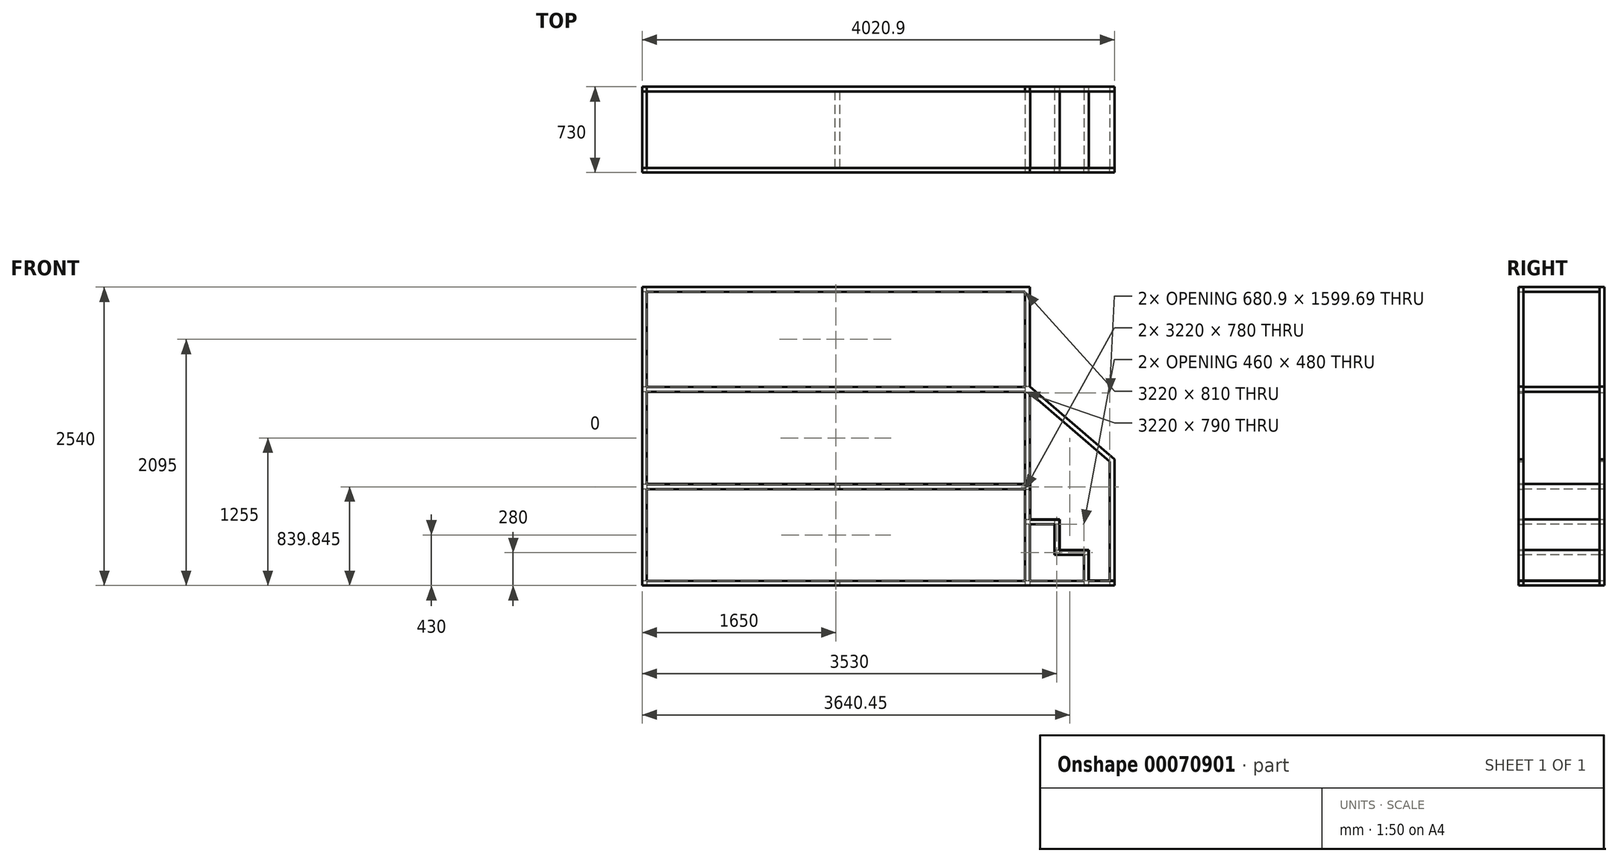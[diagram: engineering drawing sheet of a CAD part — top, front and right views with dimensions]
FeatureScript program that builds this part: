
annotation { "Feature Type Name" : "Feature", "Feature Type Description" : "" }
export const myFeature = defineFeature(function(context is Context, id is Id, definition is map)
    precondition{}
    {
        {
            var Q0;
            Q0=qCreatedBy(makeId("Front.planeOp"),FACE);
            var sketch = newSketch(context, id + "F0", { "sketchPlane" : qUnion([Q0])});
            skLineSegment(sketch, "E0", {"start": v(40, 0) * mm, "end": v(3260, 0) * mm});
            skLineSegment(sketch, "E1.0", {"start": v(40, 40) * mm, "end": v(3260, 40) * mm});
            skLineSegment(sketch, "E2", {"start": v(0, 40) * mm, "end": v(0, 0) * mm});
            skLineSegment(sketch, "E3.0", {"start": v(3300, 40) * mm, "end": v(3300, 0) * mm});
            skLineSegment(sketch, "E4", {"start": v(0, 0) * mm, "end": v(0, -820) * mm});
            skLineSegment(sketch, "E5", {"start": v(3300, 0) * mm, "end": v(3300, -260) * mm});
            skLineSegment(sketch, "E6", {"start": v(0, -820) * mm, "end": v(3300, -820) * mm});
            skLineSegment(sketch, "E7.0", {"start": v(40, -780) * mm, "end": v(3260, -780) * mm});
            skLineSegment(sketch, "E8.0", {"start": v(40, 0) * mm, "end": v(40, -780) * mm});
            skLineSegment(sketch, "E9.0", {"start": v(3260, 0) * mm, "end": v(3260, -780) * mm});
            skLineSegment(sketch, "E10", {"start": v(0, 40) * mm, "end": v(0, 1720) * mm});
            skLineSegment(sketch, "E11", {"start": v(0, 1720) * mm, "end": v(3300, 1720) * mm});
            skLineSegment(sketch, "E12", {"start": v(3300, 1720) * mm, "end": v(3300, 872.37) * mm});
            skLineSegment(sketch, "E13", {"start": v(40, 40) * mm, "end": v(40, 1680) * mm});
            skLineSegment(sketch, "E14", {"start": v(40, 1680) * mm, "end": v(3260, 1680) * mm});
            skLineSegment(sketch, "E15", {"start": v(3260, 1680) * mm, "end": v(3260, 40) * mm});
            skLineSegment(sketch, "E16", {"start": v(3300, 872.37) * mm, "end": v(4020.9, 254.57) * mm});
            skLineSegment(sketch, "E17", {"start": v(4020.9, 254.57) * mm, "end": v(4020.9, -820) * mm});
            skLineSegment(sketch, "E18", {"start": v(4020.9, -820) * mm, "end": v(3300, -820) * mm});
            skLineSegment(sketch, "E19", {"start": v(3260, -780) * mm, "end": v(3760, -780) * mm});
            skLineSegment(sketch, "E20", {"start": v(3980.9, -780) * mm, "end": v(3980.9, 236.17) * mm});
            skLineSegment(sketch, "E21", {"start": v(3980.9, 236.17) * mm, "end": v(3300, 819.7) * mm});
            skLineSegment(sketch, "E22", {"start": v(3300, -300) * mm, "end": v(3510, -300) * mm});
            skLineSegment(sketch, "E23", {"start": v(3510, -300) * mm, "end": v(3510, -560) * mm});
            skLineSegment(sketch, "E24", {"start": v(3510, -560) * mm, "end": v(3760, -560) * mm});
            skLineSegment(sketch, "E25", {"start": v(3760, -560) * mm, "end": v(3760, -780) * mm});
            skLineSegment(sketch, "E26", {"start": v(3300, -260) * mm, "end": v(3550, -260) * mm});
            skLineSegment(sketch, "E27", {"start": v(3550, -260) * mm, "end": v(3550, -520) * mm});
            skLineSegment(sketch, "E28", {"start": v(3550, -520) * mm, "end": v(3800, -520) * mm});
            skLineSegment(sketch, "E29", {"start": v(3800, -520) * mm, "end": v(3800, -780) * mm});
            skLineSegment(sketch, "E30.trimOffspring", {"start": v(3300, -300) * mm, "end": v(3300, -820) * mm});
            skLineSegment(sketch, "E31.trimOffspring", {"start": v(3800, -780) * mm, "end": v(3980.9, -780) * mm});
            skLineSegment(sketch, "E32.trimOffspring", {"start": v(3300, 819.7) * mm, "end": v(3300, 40) * mm});
            skSolve(sketch);
        }
        {
            var Q0;
            Q0=makeQuery(id+"F0.imprint","IMPRINT",FACE,{"disambiguationData":[TD([[makeQuery(id+"F0.imprint","IMPRINT",EDGE,{"derivedFrom":sQuery(id+"F0.wireOp",EDGE,"E0")}),1.0]])]});
            extrude(context, id + "F1", {"entities" : qUnion([Q0]), "depth" : 40 * mm});
        }
        {
            var Q0;
            Q0=makeQuery(id+"F1.opExtrude","CAP_FACE",FACE,{"disambiguationData":[OSD([sQuery(id+"F0.wireOp",EDGE,"E0"),sQuery(id+"F0.wireOp",EDGE,"E1.0"),sQuery(id+"F0.wireOp",EDGE,"E2"),sQuery(id+"F0.wireOp",EDGE,"E3.0"),sQuery(id+"F0.wireOp",EDGE,"E4"),sQuery(id+"F0.wireOp",EDGE,"E5"),sQuery(id+"F0.wireOp",EDGE,"E6"),sQuery(id+"F0.wireOp",EDGE,"E7.0"),sQuery(id+"F0.wireOp",EDGE,"E8.0"),sQuery(id+"F0.wireOp",EDGE,"E9.0"),sQuery(id+"F0.wireOp",EDGE,"E10"),sQuery(id+"F0.wireOp",EDGE,"E11"),sQuery(id+"F0.wireOp",EDGE,"E12"),sQuery(id+"F0.wireOp",EDGE,"E13"),sQuery(id+"F0.wireOp",EDGE,"E14"),sQuery(id+"F0.wireOp",EDGE,"E15"),sQuery(id+"F0.wireOp",EDGE,"E16"),sQuery(id+"F0.wireOp",EDGE,"E17"),sQuery(id+"F0.wireOp",EDGE,"E18"),sQuery(id+"F0.wireOp",EDGE,"E19"),sQuery(id+"F0.wireOp",EDGE,"E20"),sQuery(id+"F0.wireOp",EDGE,"E21"),sQuery(id+"F0.wireOp",EDGE,"E22"),sQuery(id+"F0.wireOp",EDGE,"E23"),sQuery(id+"F0.wireOp",EDGE,"E24"),sQuery(id+"F0.wireOp",EDGE,"E25"),sQuery(id+"F0.wireOp",EDGE,"E26"),sQuery(id+"F0.wireOp",EDGE,"E27"),sQuery(id+"F0.wireOp",EDGE,"E28"),sQuery(id+"F0.wireOp",EDGE,"E29"),sQuery(id+"F0.wireOp",EDGE,"E30.trimOffspring"),sQuery(id+"F0.wireOp",EDGE,"E31.trimOffspring"),sQuery(id+"F0.wireOp",EDGE,"E32.trimOffspring")])],"isStart":true});
            var sketch = newSketch(context, id + "F2", { "sketchPlane" : qUnion([Q0])});
            skLineSegment(sketch, "E33.bottom", {"start": v(-3260, 0) * mm, "end": v(-3300, 0) * mm});
            skLineSegment(sketch, "E33.top", {"start": v(-3260, 40) * mm, "end": v(-3300, 40) * mm});
            skLineSegment(sketch, "E33.left", {"start": v(-3260, 0) * mm, "end": v(-3260, 40) * mm});
            skLineSegment(sketch, "E33.right", {"start": v(-3300, 0) * mm, "end": v(-3300, 40) * mm});
            skLineSegment(sketch, "E34.bottom", {"start": v(-3300, -260) * mm, "end": v(-3260, -260) * mm});
            skLineSegment(sketch, "E34.top", {"start": v(-3300, -300) * mm, "end": v(-3260, -300) * mm});
            skLineSegment(sketch, "E34.left", {"start": v(-3300, -260) * mm, "end": v(-3300, -300) * mm});
            skLineSegment(sketch, "E34.right", {"start": v(-3260, -260) * mm, "end": v(-3260, -300) * mm});
            skLineSegment(sketch, "E35.bottom", {"start": v(-3550, -260) * mm, "end": v(-3510, -260) * mm});
            skLineSegment(sketch, "E35.top", {"start": v(-3550, -300) * mm, "end": v(-3510, -300) * mm});
            skLineSegment(sketch, "E35.left", {"start": v(-3550, -260) * mm, "end": v(-3550, -300) * mm});
            skLineSegment(sketch, "E35.right", {"start": v(-3510, -260) * mm, "end": v(-3510, -300) * mm});
            skLineSegment(sketch, "E36.bottom", {"start": v(-3550, -520) * mm, "end": v(-3510, -520) * mm});
            skLineSegment(sketch, "E36.top", {"start": v(-3550, -560) * mm, "end": v(-3510, -560) * mm});
            skLineSegment(sketch, "E36.left", {"start": v(-3550, -520) * mm, "end": v(-3550, -560) * mm});
            skLineSegment(sketch, "E36.right", {"start": v(-3510, -520) * mm, "end": v(-3510, -560) * mm});
            skLineSegment(sketch, "E37.bottom", {"start": v(-3800, -520) * mm, "end": v(-3760, -520) * mm});
            skLineSegment(sketch, "E37.top", {"start": v(-3800, -560) * mm, "end": v(-3760, -560) * mm});
            skLineSegment(sketch, "E37.left", {"start": v(-3800, -520) * mm, "end": v(-3800, -560) * mm});
            skLineSegment(sketch, "E37.right", {"start": v(-3760, -520) * mm, "end": v(-3760, -560) * mm});
            skLineSegment(sketch, "E38.bottom", {"start": v(-3980.9, -780) * mm, "end": v(-4020.9, -780) * mm});
            skLineSegment(sketch, "E38.top", {"start": v(-3980.9, -820) * mm, "end": v(-4020.9, -820) * mm});
            skLineSegment(sketch, "E38.left", {"start": v(-3980.9, -780) * mm, "end": v(-3980.9, -820) * mm});
            skLineSegment(sketch, "E38.right", {"start": v(-4020.9, -780) * mm, "end": v(-4020.9, -820) * mm});
            skLineSegment(sketch, "E39.bottom", {"start": v(-40, 40) * mm, "end": v(0, 40) * mm});
            skLineSegment(sketch, "E39.top", {"start": v(-40, 0) * mm, "end": v(0, 0) * mm});
            skLineSegment(sketch, "E39.left", {"start": v(-40, 40) * mm, "end": v(-40, 0) * mm});
            skLineSegment(sketch, "E39.right", {"start": v(0, 40) * mm, "end": v(0, 0) * mm});
            skLineSegment(sketch, "E40.bottom", {"start": v(-40, -780) * mm, "end": v(0, -780) * mm});
            skLineSegment(sketch, "E40.top", {"start": v(-40, -820) * mm, "end": v(0, -820) * mm});
            skLineSegment(sketch, "E40.left", {"start": v(-40, -780) * mm, "end": v(-40, -820) * mm});
            skLineSegment(sketch, "E40.right", {"start": v(0, -780) * mm, "end": v(0, -820) * mm});
            skLineSegment(sketch, "E41.bottom", {"start": v(-3800, -780) * mm, "end": v(-3760, -780) * mm});
            skLineSegment(sketch, "E41.top", {"start": v(-3800, -820) * mm, "end": v(-3760, -820) * mm});
            skLineSegment(sketch, "E41.left", {"start": v(-3800, -780) * mm, "end": v(-3800, -820) * mm});
            skLineSegment(sketch, "E41.right", {"start": v(-3760, -780) * mm, "end": v(-3760, -820) * mm});
            skLineSegment(sketch, "E42.bottom", {"start": v(-3300, -780) * mm, "end": v(-3260, -780) * mm});
            skLineSegment(sketch, "E42.top", {"start": v(-3300, -820) * mm, "end": v(-3260, -820) * mm});
            skLineSegment(sketch, "E42.left", {"start": v(-3300, -780) * mm, "end": v(-3300, -820) * mm});
            skLineSegment(sketch, "E42.right", {"start": v(-3260, -780) * mm, "end": v(-3260, -820) * mm});
            skLineSegment(sketch, "E43.bottom", {"start": v(-1680, 40) * mm, "end": v(-1640, 40) * mm});
            skLineSegment(sketch, "E43.top", {"start": v(-1680, 0) * mm, "end": v(-1640, 0) * mm});
            skLineSegment(sketch, "E43.left", {"start": v(-1680, 40) * mm, "end": v(-1680, 0) * mm});
            skLineSegment(sketch, "E43.right", {"start": v(-1640, 40) * mm, "end": v(-1640, 0) * mm});
            skLineSegment(sketch, "E44.bottom", {"start": v(-1680, -780) * mm, "end": v(-1640, -780) * mm});
            skLineSegment(sketch, "E44.top", {"start": v(-1680, -820) * mm, "end": v(-1640, -820) * mm});
            skLineSegment(sketch, "E44.left", {"start": v(-1680, -780) * mm, "end": v(-1680, -820) * mm});
            skLineSegment(sketch, "E44.right", {"start": v(-1640, -780) * mm, "end": v(-1640, -820) * mm});
            skLineSegment(sketch, "E45.bottom", {"start": v(-40, 1680) * mm, "end": v(0, 1680) * mm});
            skLineSegment(sketch, "E45.top", {"start": v(-40, 1720) * mm, "end": v(0, 1720) * mm});
            skLineSegment(sketch, "E45.left", {"start": v(-40, 1680) * mm, "end": v(-40, 1720) * mm});
            skLineSegment(sketch, "E45.right", {"start": v(0, 1680) * mm, "end": v(0, 1720) * mm});
            skSolve(sketch);
        }
        {
            var Q0;
            Q0=makeQuery(id+"F2.imprint","IMPRINT",FACE,{"disambiguationData":[TD([[makeQuery(id+"F2.imprint","IMPRINT",EDGE,{"derivedFrom":sQuery(id+"F2.wireOp",EDGE,"E45.bottom")}),1.0]])]});
            var Q1;
            Q1=makeQuery(id+"F2.imprint","IMPRINT",FACE,{"disambiguationData":[TD([[makeQuery(id+"F2.imprint","IMPRINT",EDGE,{"derivedFrom":sQuery(id+"F2.wireOp",EDGE,"E39.bottom")}),-1.0]])]});
            var Q2;
            Q2=makeQuery(id+"F2.imprint","IMPRINT",FACE,{"disambiguationData":[TD([[makeQuery(id+"F2.imprint","IMPRINT",EDGE,{"derivedFrom":sQuery(id+"F2.wireOp",EDGE,"E40.bottom")}),-1.0]])]});
            var Q3;
            Q3=makeQuery(id+"F2.imprint","IMPRINT",FACE,{"disambiguationData":[TD([[makeQuery(id+"F2.imprint","IMPRINT",EDGE,{"derivedFrom":sQuery(id+"F2.wireOp",EDGE,"E44.bottom")}),1.0]])]});
            var Q4;
            Q4=makeQuery(id+"F2.imprint","IMPRINT",FACE,{"disambiguationData":[TD([[makeQuery(id+"F2.imprint","IMPRINT",EDGE,{"derivedFrom":sQuery(id+"F2.wireOp",EDGE,"E43.bottom")}),1.0]])]});
            var Q5;
            Q5=makeQuery(id+"F2.imprint","IMPRINT",FACE,{"disambiguationData":[TD([[makeQuery(id+"F2.imprint","IMPRINT",EDGE,{"derivedFrom":sQuery(id+"F2.wireOp",EDGE,"E33.bottom")}),-1.0]])]});
            var Q6;
            Q6=makeQuery(id+"F2.imprint","IMPRINT",FACE,{"disambiguationData":[TD([[makeQuery(id+"F2.imprint","IMPRINT",EDGE,{"derivedFrom":sQuery(id+"F2.wireOp",EDGE,"E42.bottom")}),-1.0]])]});
            var Q7;
            Q7=makeQuery(id+"F2.imprint","IMPRINT",FACE,{"disambiguationData":[TD([[makeQuery(id+"F2.imprint","IMPRINT",EDGE,{"derivedFrom":sQuery(id+"F2.wireOp",EDGE,"E34.bottom")}),-1.0]])]});
            var Q8;
            Q8=makeQuery(id+"F2.imprint","IMPRINT",FACE,{"disambiguationData":[TD([[makeQuery(id+"F2.imprint","IMPRINT",EDGE,{"derivedFrom":sQuery(id+"F2.wireOp",EDGE,"E35.bottom")}),1.0]])]});
            var Q9;
            Q9=makeQuery(id+"F2.imprint","IMPRINT",FACE,{"disambiguationData":[TD([[makeQuery(id+"F2.imprint","IMPRINT",EDGE,{"derivedFrom":sQuery(id+"F2.wireOp",EDGE,"E37.bottom")}),1.0]])]});
            var Q10;
            Q10=makeQuery(id+"F2.imprint","IMPRINT",FACE,{"disambiguationData":[TD([[makeQuery(id+"F2.imprint","IMPRINT",EDGE,{"derivedFrom":sQuery(id+"F2.wireOp",EDGE,"E36.bottom")}),-1.0]])]});
            var Q11;
            Q11=makeQuery(id+"F2.imprint","IMPRINT",FACE,{"disambiguationData":[TD([[makeQuery(id+"F2.imprint","IMPRINT",EDGE,{"derivedFrom":sQuery(id+"F2.wireOp",EDGE,"E41.bottom")}),-1.0]])]});
            var Q12;
            Q12=makeQuery(id+"F2.imprint","IMPRINT",FACE,{"disambiguationData":[TD([[makeQuery(id+"F2.imprint","IMPRINT",EDGE,{"derivedFrom":sQuery(id+"F2.wireOp",EDGE,"E38.bottom")}),1.0]])]});
            extrude(context, id + "F3", {"entities" : qUnion([Q0, Q1, Q2, Q3, Q4, Q5, Q6, Q7, Q8, Q9, Q10, Q11, Q12]), "depth" : 650 * mm});
        }
        {
            var Q0;
            Q0=makeQuery(id+"F1.opExtrude","CAP_FACE",FACE,{"disambiguationData":[OSD([sQuery(id+"F0.wireOp",EDGE,"E0"),sQuery(id+"F0.wireOp",EDGE,"E1.0"),sQuery(id+"F0.wireOp",EDGE,"E2"),sQuery(id+"F0.wireOp",EDGE,"E3.0"),sQuery(id+"F0.wireOp",EDGE,"E4"),sQuery(id+"F0.wireOp",EDGE,"E5"),sQuery(id+"F0.wireOp",EDGE,"E6"),sQuery(id+"F0.wireOp",EDGE,"E7.0"),sQuery(id+"F0.wireOp",EDGE,"E8.0"),sQuery(id+"F0.wireOp",EDGE,"E9.0"),sQuery(id+"F0.wireOp",EDGE,"E10"),sQuery(id+"F0.wireOp",EDGE,"E11"),sQuery(id+"F0.wireOp",EDGE,"E12"),sQuery(id+"F0.wireOp",EDGE,"E13"),sQuery(id+"F0.wireOp",EDGE,"E14"),sQuery(id+"F0.wireOp",EDGE,"E15"),sQuery(id+"F0.wireOp",EDGE,"E16"),sQuery(id+"F0.wireOp",EDGE,"E17"),sQuery(id+"F0.wireOp",EDGE,"E18"),sQuery(id+"F0.wireOp",EDGE,"E19"),sQuery(id+"F0.wireOp",EDGE,"E20"),sQuery(id+"F0.wireOp",EDGE,"E21"),sQuery(id+"F0.wireOp",EDGE,"E22"),sQuery(id+"F0.wireOp",EDGE,"E23"),sQuery(id+"F0.wireOp",EDGE,"E24"),sQuery(id+"F0.wireOp",EDGE,"E25"),sQuery(id+"F0.wireOp",EDGE,"E26"),sQuery(id+"F0.wireOp",EDGE,"E27"),sQuery(id+"F0.wireOp",EDGE,"E28"),sQuery(id+"F0.wireOp",EDGE,"E29"),sQuery(id+"F0.wireOp",EDGE,"E30.trimOffspring"),sQuery(id+"F0.wireOp",EDGE,"E31.trimOffspring"),sQuery(id+"F0.wireOp",EDGE,"E32.trimOffspring")])],"isStart":true});
            cPlane(context, id + "F4", {"entities" : qUnion([Q0]), "cplaneType" : CPlaneType.OFFSET, "offset" : 325 * mm, "width" : 150 * mm, "height" : 150 * mm});
        }
        {
            var Q0;
            Q0=makeQuery(id+"F1.opExtrude","SWEPT_BODY",BODY,{"disambiguationData":[OSD([sQuery(id+"F0.wireOp",EDGE,"E0"),sQuery(id+"F0.wireOp",EDGE,"E1.0"),sQuery(id+"F0.wireOp",EDGE,"E2"),sQuery(id+"F0.wireOp",EDGE,"E3.0"),sQuery(id+"F0.wireOp",EDGE,"E4"),sQuery(id+"F0.wireOp",EDGE,"E5"),sQuery(id+"F0.wireOp",EDGE,"E6"),sQuery(id+"F0.wireOp",EDGE,"E7.0"),sQuery(id+"F0.wireOp",EDGE,"E8.0"),sQuery(id+"F0.wireOp",EDGE,"E9.0"),sQuery(id+"F0.wireOp",EDGE,"E10"),sQuery(id+"F0.wireOp",EDGE,"E11"),sQuery(id+"F0.wireOp",EDGE,"E12"),sQuery(id+"F0.wireOp",EDGE,"E13"),sQuery(id+"F0.wireOp",EDGE,"E14"),sQuery(id+"F0.wireOp",EDGE,"E15"),sQuery(id+"F0.wireOp",EDGE,"E16"),sQuery(id+"F0.wireOp",EDGE,"E17"),sQuery(id+"F0.wireOp",EDGE,"E18"),sQuery(id+"F0.wireOp",EDGE,"E19"),sQuery(id+"F0.wireOp",EDGE,"E20"),sQuery(id+"F0.wireOp",EDGE,"E21"),sQuery(id+"F0.wireOp",EDGE,"E22"),sQuery(id+"F0.wireOp",EDGE,"E23"),sQuery(id+"F0.wireOp",EDGE,"E24"),sQuery(id+"F0.wireOp",EDGE,"E25"),sQuery(id+"F0.wireOp",EDGE,"E26"),sQuery(id+"F0.wireOp",EDGE,"E27"),sQuery(id+"F0.wireOp",EDGE,"E28"),sQuery(id+"F0.wireOp",EDGE,"E29"),sQuery(id+"F0.wireOp",EDGE,"E30.trimOffspring"),sQuery(id+"F0.wireOp",EDGE,"E31.trimOffspring"),sQuery(id+"F0.wireOp",EDGE,"E32.trimOffspring")])]});
            var Q1;
            Q1=qCreatedBy(id+"F4.planeOp",FACE);
            mirror(context, id + "F5", {"entities" : qUnion([Q0]), "mirrorPlane" : qUnion([Q1])});
        }
        {
            var Q0;
            Q0=makeQuery(id+"F1.opExtrude","CAP_FACE",FACE,{"disambiguationData":[OSD([sQuery(id+"F0.wireOp",EDGE,"E0"),sQuery(id+"F0.wireOp",EDGE,"E1.0"),sQuery(id+"F0.wireOp",EDGE,"E2"),sQuery(id+"F0.wireOp",EDGE,"E3.0"),sQuery(id+"F0.wireOp",EDGE,"E4"),sQuery(id+"F0.wireOp",EDGE,"E5"),sQuery(id+"F0.wireOp",EDGE,"E6"),sQuery(id+"F0.wireOp",EDGE,"E7.0"),sQuery(id+"F0.wireOp",EDGE,"E8.0"),sQuery(id+"F0.wireOp",EDGE,"E9.0"),sQuery(id+"F0.wireOp",EDGE,"E10"),sQuery(id+"F0.wireOp",EDGE,"E11"),sQuery(id+"F0.wireOp",EDGE,"E12"),sQuery(id+"F0.wireOp",EDGE,"E13"),sQuery(id+"F0.wireOp",EDGE,"E14"),sQuery(id+"F0.wireOp",EDGE,"E15"),sQuery(id+"F0.wireOp",EDGE,"E16"),sQuery(id+"F0.wireOp",EDGE,"E17"),sQuery(id+"F0.wireOp",EDGE,"E18"),sQuery(id+"F0.wireOp",EDGE,"E19"),sQuery(id+"F0.wireOp",EDGE,"E20"),sQuery(id+"F0.wireOp",EDGE,"E21"),sQuery(id+"F0.wireOp",EDGE,"E22"),sQuery(id+"F0.wireOp",EDGE,"E23"),sQuery(id+"F0.wireOp",EDGE,"E24"),sQuery(id+"F0.wireOp",EDGE,"E25"),sQuery(id+"F0.wireOp",EDGE,"E26"),sQuery(id+"F0.wireOp",EDGE,"E27"),sQuery(id+"F0.wireOp",EDGE,"E28"),sQuery(id+"F0.wireOp",EDGE,"E29"),sQuery(id+"F0.wireOp",EDGE,"E30.trimOffspring"),sQuery(id+"F0.wireOp",EDGE,"E31.trimOffspring"),sQuery(id+"F0.wireOp",EDGE,"E32.trimOffspring")])],"isStart":false});
            var sketch = newSketch(context, id + "F6", { "sketchPlane" : qUnion([Q0])});
            skLineSegment(sketch, "E46", {"start": v(40, 40) * mm, "end": v(3300, 40) * mm});
            skLineSegment(sketch, "E47", {"start": v(3300, 40) * mm, "end": v(3300, -260) * mm});
            skLineSegment(sketch, "E48", {"start": v(3300, -260) * mm, "end": v(3550, -260) * mm});
            skLineSegment(sketch, "E49", {"start": v(3550, -260) * mm, "end": v(3550, -520) * mm});
            skLineSegment(sketch, "E50", {"start": v(3550, -520) * mm, "end": v(3800, -520) * mm});
            skLineSegment(sketch, "E51", {"start": v(3800, -520) * mm, "end": v(3800, -780) * mm});
            skLineSegment(sketch, "E52", {"start": v(3800, -780) * mm, "end": v(4020.9, -780) * mm});
            skLineSegment(sketch, "E53.0", {"start": v(3803, -777) * mm, "end": v(4020.9, -777) * mm});
            skLineSegment(sketch, "E53.1", {"start": v(3803, -517) * mm, "end": v(3803, -777) * mm});
            skLineSegment(sketch, "E53.2", {"start": v(3553, -517) * mm, "end": v(3803, -517) * mm});
            skLineSegment(sketch, "E53.3", {"start": v(40, 43) * mm, "end": v(3303, 43) * mm});
            skLineSegment(sketch, "E53.4", {"start": v(3303, 43) * mm, "end": v(3303, -257) * mm});
            skLineSegment(sketch, "E53.5", {"start": v(3303, -257) * mm, "end": v(3553, -257) * mm});
            skLineSegment(sketch, "E53.6", {"start": v(3553, -257) * mm, "end": v(3553, -517) * mm});
            skLineSegment(sketch, "E54", {"start": v(4020.9, -777) * mm, "end": v(4020.9, -780) * mm});
            skLineSegment(sketch, "E55", {"start": v(40, 43) * mm, "end": v(40, 40) * mm});
            skSolve(sketch);
        }
        {
            var Q0;
            {var subQ0=sQuery(id+"F6.wireOp",EDGE,"E55");Q0=makeQuery(id+"F6.imprint","IMPRINT",FACE,{"disambiguationData":[TD([[makeQuery(id+"F6.imprint","IMPRINT",EDGE,{"derivedFrom":subQ0}),-1.0]])]});}
            var Q1;
            {var subQ0=sQuery(id+"F6.wireOp",EDGE,"E46");var subQ1=makeQuery(id+"F1.opExtrude","CAP_EDGE",EDGE,{"disambiguationData":[OSD([sQuery(id+"F0.wireOp",EDGE,"E15")])],"isStart":false});var subQ2=makeQuery(id+"F6.imprint","INTERSECT",VERTEX,{"derivedFrom":[subQ1,subQ0]});Q1=makeQuery(id+"F6.imprint","IMPRINT",FACE,{"disambiguationData":[TD([[makeQuery(id+"F6.imprint","IMPRINT",EDGE,{"disambiguationData":[TD([[subQ2,1.0]])],"derivedFrom":subQ1}),1.0]])]});}
            var Q2;
            {var subQ11=sQuery(id+"F6.wireOp",EDGE,"E47");Q2=makeQuery(id+"F6.imprint","IMPRINT",FACE,{"disambiguationData":[TD([[makeQuery(id+"F6.imprint","IMPRINT",EDGE,{"derivedFrom":subQ11}),1.0]])]});}
            var Q3;
            {var subQ3=sQuery(id+"F6.wireOp",EDGE,"E54");Q3=makeQuery(id+"F6.imprint","IMPRINT",FACE,{"disambiguationData":[TD([[makeQuery(id+"F6.imprint","IMPRINT",EDGE,{"derivedFrom":subQ3}),-1.0]])]});}
            extrude(context, id + "F7", {"entities" : qUnion([Q0, Q1, Q2, Q3]), "oppositeDirection" : true, "depth" : 690 * mm});
        }
        {
            var Q0;
            Q0=makeQuery(id+"F5.opPattern","COPY",FACE,{"derivedFrom":makeQuery(id+"F1.opExtrude","CAP_FACE",FACE,{"disambiguationData":[OSD([sQuery(id+"F0.wireOp",EDGE,"E0"),sQuery(id+"F0.wireOp",EDGE,"E1.0"),sQuery(id+"F0.wireOp",EDGE,"E2"),sQuery(id+"F0.wireOp",EDGE,"E3.0"),sQuery(id+"F0.wireOp",EDGE,"E4"),sQuery(id+"F0.wireOp",EDGE,"E5"),sQuery(id+"F0.wireOp",EDGE,"E6"),sQuery(id+"F0.wireOp",EDGE,"E7.0"),sQuery(id+"F0.wireOp",EDGE,"E8.0"),sQuery(id+"F0.wireOp",EDGE,"E9.0"),sQuery(id+"F0.wireOp",EDGE,"E10"),sQuery(id+"F0.wireOp",EDGE,"E11"),sQuery(id+"F0.wireOp",EDGE,"E12"),sQuery(id+"F0.wireOp",EDGE,"E13"),sQuery(id+"F0.wireOp",EDGE,"E14"),sQuery(id+"F0.wireOp",EDGE,"E15"),sQuery(id+"F0.wireOp",EDGE,"E16"),sQuery(id+"F0.wireOp",EDGE,"E17"),sQuery(id+"F0.wireOp",EDGE,"E18"),sQuery(id+"F0.wireOp",EDGE,"E19"),sQuery(id+"F0.wireOp",EDGE,"E20"),sQuery(id+"F0.wireOp",EDGE,"E21"),sQuery(id+"F0.wireOp",EDGE,"E22"),sQuery(id+"F0.wireOp",EDGE,"E23"),sQuery(id+"F0.wireOp",EDGE,"E24"),sQuery(id+"F0.wireOp",EDGE,"E25"),sQuery(id+"F0.wireOp",EDGE,"E26"),sQuery(id+"F0.wireOp",EDGE,"E27"),sQuery(id+"F0.wireOp",EDGE,"E28"),sQuery(id+"F0.wireOp",EDGE,"E29"),sQuery(id+"F0.wireOp",EDGE,"E30.trimOffspring"),sQuery(id+"F0.wireOp",EDGE,"E31.trimOffspring"),sQuery(id+"F0.wireOp",EDGE,"E32.trimOffspring")])],"isStart":false}),"instanceName":"1"});
            var sketch = newSketch(context, id + "F8", { "sketchPlane" : qUnion([Q0])});
            skLineSegment(sketch, "E56.bottom", {"start": v(-3300, 1720) * mm, "end": v(-40, 1720) * mm});
            skLineSegment(sketch, "E56.top", {"start": v(-3300, 1680) * mm, "end": v(0, 1680) * mm});
            skLineSegment(sketch, "E56.left", {"start": v(-3300, 1720) * mm, "end": v(-3300, 1680) * mm});
            skLineSegment(sketch, "E56.right", {"start": v(-40, 1720) * mm, "end": v(-40, 1680) * mm});
            skLineSegment(sketch, "E57", {"start": v(-3300, 1680) * mm, "end": v(-3300, 872.37) * mm});
            skLineSegment(sketch, "E58", {"start": v(-3300, 872.37) * mm, "end": v(-3260, 872.37) * mm});
            skLineSegment(sketch, "E59", {"start": v(-3260, 872.37) * mm, "end": v(-3260, 1680) * mm});
            skSolve(sketch);
        }
        {
            var Q0;
            Q0=makeQuery(id+"F8.imprint","IMPRINT",FACE,{"disambiguationData":[TD([[makeQuery(id+"F8.imprint","IMPRINT",EDGE,{"derivedFrom":sQuery(id+"F8.wireOp",EDGE,"E56.bottom")}),1.0]])]});
            var Q1;
            {var subQ2=sQuery(id+"F8.wireOp",EDGE,"E57");Q1=makeQuery(id+"F8.imprint","IMPRINT",FACE,{"disambiguationData":[TD([[makeQuery(id+"F8.imprint","IMPRINT",EDGE,{"derivedFrom":subQ2}),1.0]])]});}
            extrude(context, id + "F9", {"entities" : qUnion([Q0, Q1]), "operationType" : NewBodyOperationType.REMOVE, "oppositeDirection" : true, "depth" : 40 * mm});
        }
        {
            var Q0;
            Q0=makeQuery(id+"F1.opExtrude","CAP_FACE",FACE,{"disambiguationData":[OSD([sQuery(id+"F0.wireOp",EDGE,"E0"),sQuery(id+"F0.wireOp",EDGE,"E1.0"),sQuery(id+"F0.wireOp",EDGE,"E2"),sQuery(id+"F0.wireOp",EDGE,"E3.0"),sQuery(id+"F0.wireOp",EDGE,"E4"),sQuery(id+"F0.wireOp",EDGE,"E5"),sQuery(id+"F0.wireOp",EDGE,"E6"),sQuery(id+"F0.wireOp",EDGE,"E7.0"),sQuery(id+"F0.wireOp",EDGE,"E8.0"),sQuery(id+"F0.wireOp",EDGE,"E9.0"),sQuery(id+"F0.wireOp",EDGE,"E10"),sQuery(id+"F0.wireOp",EDGE,"E11"),sQuery(id+"F0.wireOp",EDGE,"E12"),sQuery(id+"F0.wireOp",EDGE,"E13"),sQuery(id+"F0.wireOp",EDGE,"E14"),sQuery(id+"F0.wireOp",EDGE,"E15"),sQuery(id+"F0.wireOp",EDGE,"E16"),sQuery(id+"F0.wireOp",EDGE,"E17"),sQuery(id+"F0.wireOp",EDGE,"E18"),sQuery(id+"F0.wireOp",EDGE,"E19"),sQuery(id+"F0.wireOp",EDGE,"E20"),sQuery(id+"F0.wireOp",EDGE,"E21"),sQuery(id+"F0.wireOp",EDGE,"E22"),sQuery(id+"F0.wireOp",EDGE,"E23"),sQuery(id+"F0.wireOp",EDGE,"E24"),sQuery(id+"F0.wireOp",EDGE,"E25"),sQuery(id+"F0.wireOp",EDGE,"E26"),sQuery(id+"F0.wireOp",EDGE,"E27"),sQuery(id+"F0.wireOp",EDGE,"E28"),sQuery(id+"F0.wireOp",EDGE,"E29"),sQuery(id+"F0.wireOp",EDGE,"E30.trimOffspring"),sQuery(id+"F0.wireOp",EDGE,"E31.trimOffspring"),sQuery(id+"F0.wireOp",EDGE,"E32.trimOffspring")])],"isStart":false});
            var sketch = newSketch(context, id + "F10", { "sketchPlane" : qUnion([Q0])});
            skLineSegment(sketch, "E60", {"start": v(0, 870) * mm, "end": v(3270.55, 870) * mm});
            skLineSegment(sketch, "E61.0", {"start": v(0, 830) * mm, "end": v(3270.55, 830) * mm});
            skLineSegment(sketch, "E62", {"start": v(3270.55, 870) * mm, "end": v(3270.55, 830) * mm});
            skSolve(sketch);
        }
        {
            var Q0;
            {var subQ0=sQuery(id+"F10.wireOp",EDGE,"E60");var subQ1=makeQuery(id+"F1.opExtrude","CAP_EDGE",EDGE,{"disambiguationData":[OSD([sQuery(id+"F0.wireOp",EDGE,"E13")])],"isStart":false});var subQ2=makeQuery(id+"F10.imprint","INTERSECT",VERTEX,{"derivedFrom":[subQ1,subQ0]});Q0=makeQuery(id+"F10.imprint","IMPRINT",FACE,{"disambiguationData":[TD([[makeQuery(id+"F10.imprint","IMPRINT",EDGE,{"disambiguationData":[TD([[subQ2,-1.0]])],"derivedFrom":subQ0}),-1.0]])]});}
            extrude(context, id + "F11", {"entities" : qUnion([Q0]), "operationType" : NewBodyOperationType.ADD, "oppositeDirection" : true, "depth" : 40 * mm});
        }
        {
            var Q0;
            Q0=makeQuery(id+"F1.opExtrude","SWEPT_FACE",FACE,{"disambiguationData":[OSD([sQuery(id+"F0.wireOp",EDGE,"E2"),sQuery(id+"F0.wireOp",EDGE,"E4"),sQuery(id+"F0.wireOp",EDGE,"E10")])]});
            var sketch = newSketch(context, id + "F12", { "sketchPlane" : qUnion([Q0])});
            skLineSegment(sketch, "E63", {"start": v(0, 870) * mm, "end": v(-664.21, 870) * mm});
            skLineSegment(sketch, "E64", {"start": v(-664.21, 870) * mm, "end": v(-664.21, 830) * mm});
            skLineSegment(sketch, "E65", {"start": v(-664.21, 830) * mm, "end": v(0, 830) * mm});
            skLineSegment(sketch, "E66", {"start": v(0, 870) * mm, "end": v(0, 830) * mm});
            skSolve(sketch);
        }
        {
            var Q0;
            Q0=makeQuery(id+"F12.imprint","IMPRINT",FACE,{"disambiguationData":[TD([[makeQuery(id+"F12.imprint","IMPRINT",EDGE,{"derivedFrom":sQuery(id+"F12.wireOp",EDGE,"E63")}),1.0]])]});
            extrude(context, id + "F13", {"entities" : qUnion([Q0]), "operationType" : NewBodyOperationType.ADD, "oppositeDirection" : true, "depth" : 40 * mm});
        }
    });
